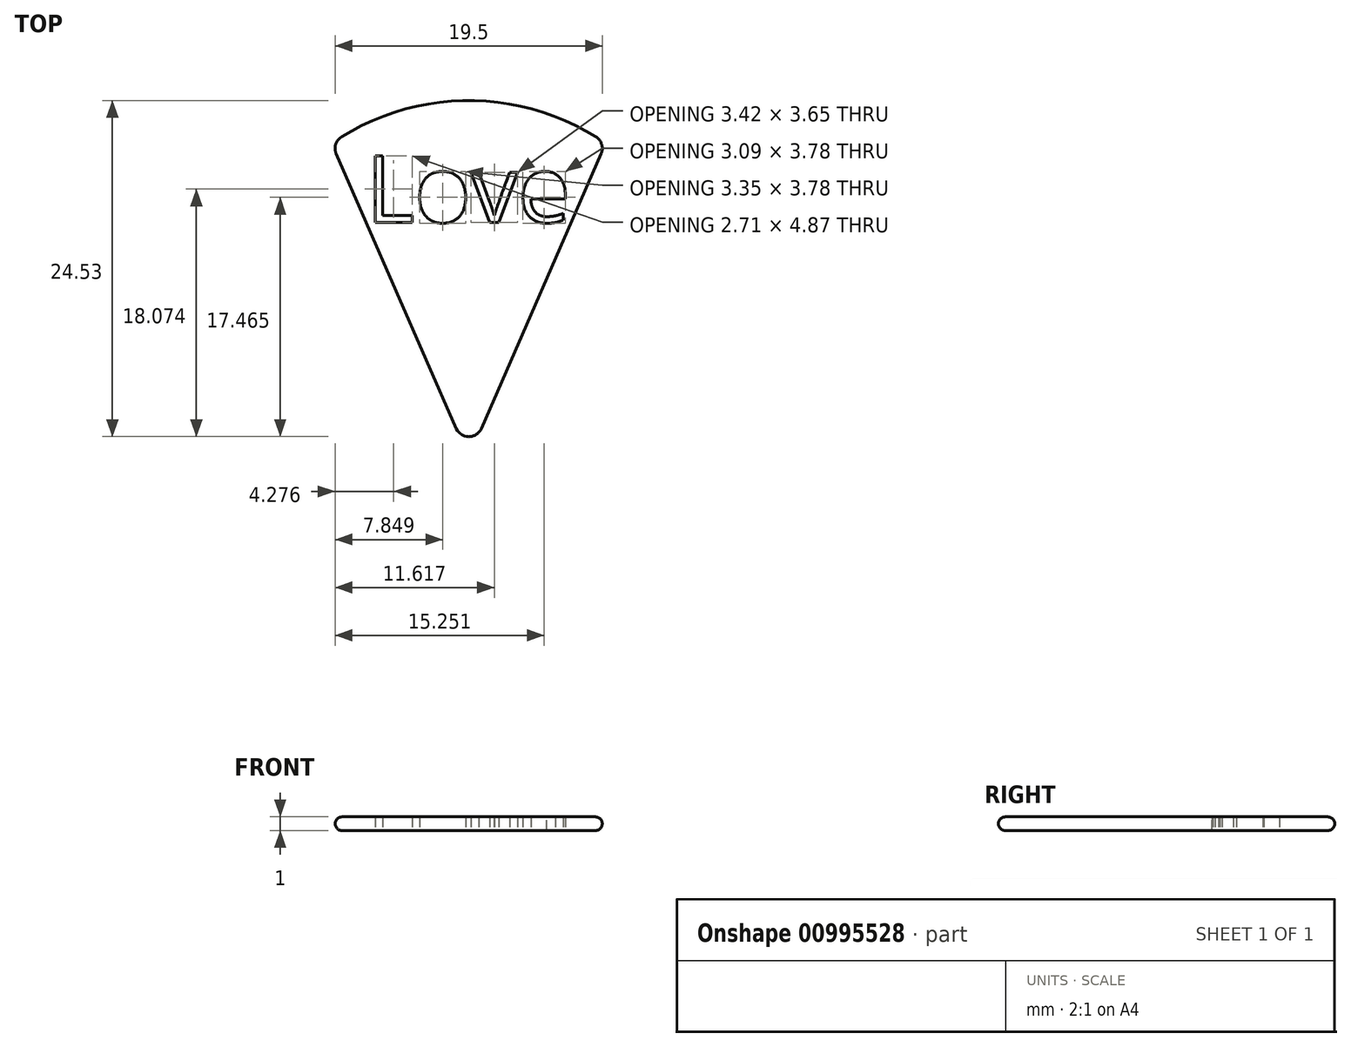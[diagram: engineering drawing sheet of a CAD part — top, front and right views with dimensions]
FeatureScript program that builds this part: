
annotation { "Feature Type Name" : "Feature", "Feature Type Description" : "" }
export const myFeature = defineFeature(function(context is Context, id is Id, definition is map)
    precondition{}
    {
        {
            var Q0;
            Q0=qCreatedBy(makeId("Top.planeOp"),FACE);
            var sketch = newSketch(context, id + "F0", { "sketchPlane" : qUnion([Q0])});
            skLineSegment(sketch, "E0", {"start": v(9.66, -0.77) * mm, "end": v(0.92, -20.81) * mm});
            skLineSegment(sketch, "E1", {"start": v(-0.92, -20.81) * mm, "end": v(-9.66, -0.77) * mm});
            skText(sketch, "E2", { "text": "Love", "fontName": "OpenSans-Regular.ttf"});
            skArc(sketch, "E3", {"start": v(9.27, 0.48) * mm, "mid": v(0, 3.12) * mm, "end": v(-9.27, 0.48) * mm});
            skPoint(sketch, "E4.visualSharp", {"position": v(-10, 0) * mm});
            skArc(sketch, "E4.filletArc", {"start": v(-9.27, 0.48) * mm, "mid": v(-9.7, -0.08) * mm, "end": v(-9.66, -0.77) * mm});
            skPoint(sketch, "E5.visualSharp", {"position": v(10, 0) * mm});
            skArc(sketch, "E5.filletArc", {"start": v(9.66, -0.77) * mm, "mid": v(9.7, -0.08) * mm, "end": v(9.27, 0.48) * mm});
            skPoint(sketch, "E6.visualSharp", {"position": v(0, -22.91) * mm});
            skArc(sketch, "E6.filletArc", {"start": v(-0.92, -20.81) * mm, "mid": v(0, -21.41) * mm, "end": v(0.92, -20.81) * mm});
            const initialGuessF0  = {"E2": [-0.0075, -0.00577, 1, 0, 0.00491]};
            skSetInitialGuess(sketch, initialGuessF0);
            skSolve(sketch);
        }
        {
            var Q0;
            Q0 = qSketchRegion(id + "F0", true);
            extrude(context, id + "F1", {"entities" : qUnion([Q0]), "depth" : 1 * mm, "offsetDistance" : 25 * mm});
        }
        {
            var Q0;
            Q0=makeQuery(id+"F1.opExtrude","CAP_EDGE",EDGE,{"disambiguationData":[OSD([sQuery(id+"F0.wireOp",EDGE,"E6.filletArc")])],"isStart":false});
            var Q1;
            Q1=makeQuery(id+"F1.opExtrude","CAP_EDGE",EDGE,{"disambiguationData":[OSD([sQuery(id+"F0.wireOp",EDGE,"E6.filletArc")])],"isStart":true});
            fillet(context, id + "F2", {"entities" : qUnion([Q0, Q1]), "radius" : 0.5 * mm, "tangentPropagation" : true, "allowEdgeOverflow" : false});
        }
    });
